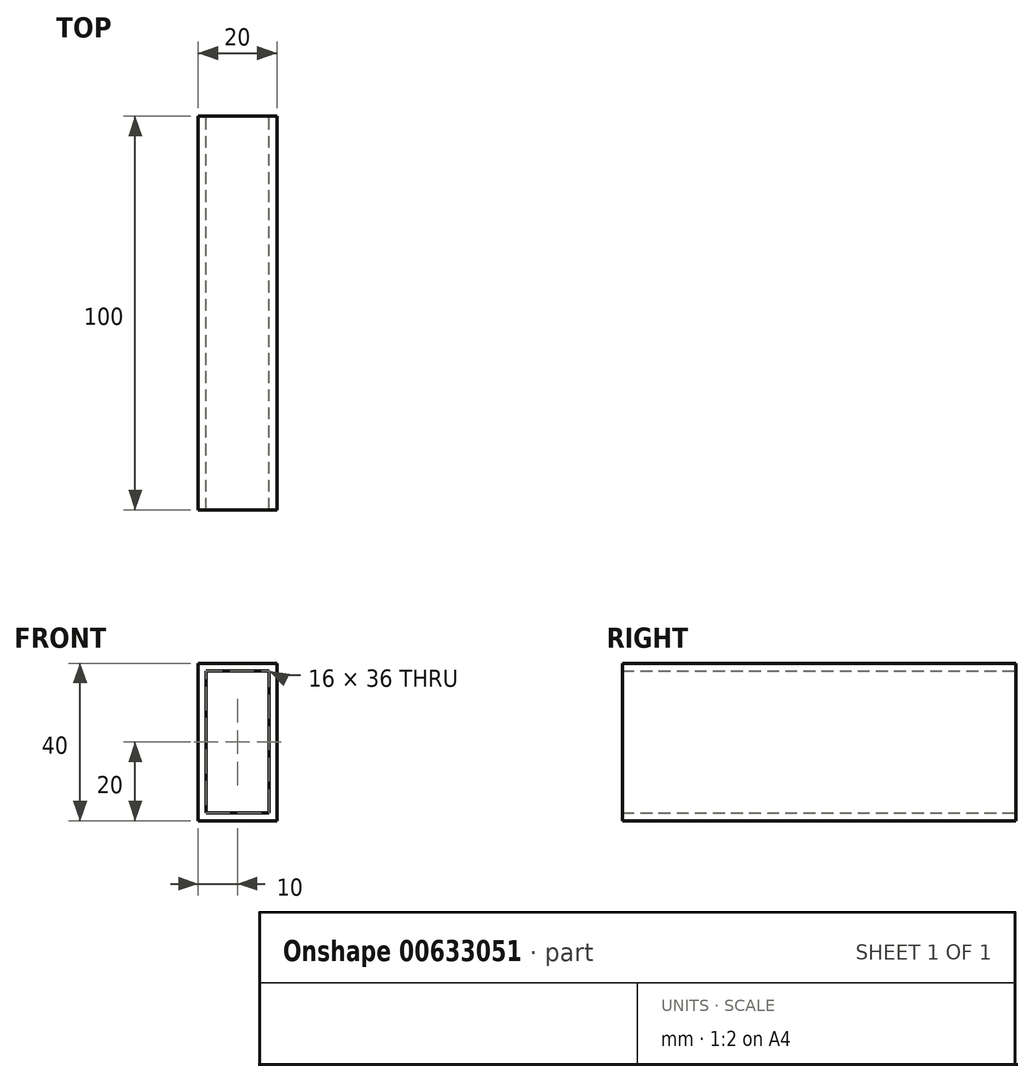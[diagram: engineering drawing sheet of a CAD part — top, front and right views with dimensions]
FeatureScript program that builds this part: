
annotation { "Feature Type Name" : "Feature", "Feature Type Description" : "" }
export const myFeature = defineFeature(function(context is Context, id is Id, definition is map)
    precondition{}
    {
        {
            var Q0;
            Q0=qCreatedBy(makeId("Front.planeOp"),FACE);
            var sketch = newSketch(context, id + "F0", { "sketchPlane" : qUnion([Q0])});
            skLineSegment(sketch, "E0.bottom", {"start": v(10, -20) * mm, "end": v(-10, -20) * mm});
            skLineSegment(sketch, "E0.top", {"start": v(10, 20) * mm, "end": v(-10, 20) * mm});
            skLineSegment(sketch, "E0.left", {"start": v(10, -20) * mm, "end": v(10, 20) * mm});
            skLineSegment(sketch, "E0.right", {"start": v(-10, -20) * mm, "end": v(-10, 20) * mm});
            skPoint(sketch, "E0.middle", {"position": v(0, 0) * mm});
            skLineSegment(sketch, "E1.0", {"start": v(8, 18) * mm, "end": v(-8, 18) * mm});
            skLineSegment(sketch, "E1.1", {"start": v(8, -18) * mm, "end": v(8, 18) * mm});
            skLineSegment(sketch, "E1.2", {"start": v(8, -18) * mm, "end": v(-8, -18) * mm});
            skLineSegment(sketch, "E1.3", {"start": v(-8, -18) * mm, "end": v(-8, 18) * mm});
            skSolve(sketch);
        }
        {
            var Q0;
            Q0=makeQuery(id+"F0.imprint","IMPRINT",FACE,{"disambiguationData":[TD([[makeQuery(id+"F0.imprint","IMPRINT",EDGE,{"derivedFrom":sQuery(id+"F0.wireOp",EDGE,"E0.bottom")}),-1.0]])]});
            extrude(context, id + "F1", {"entities" : qUnion([Q0]), "depth" : 100 * mm, "offsetDistance" : 25 * mm});
        }
    });
